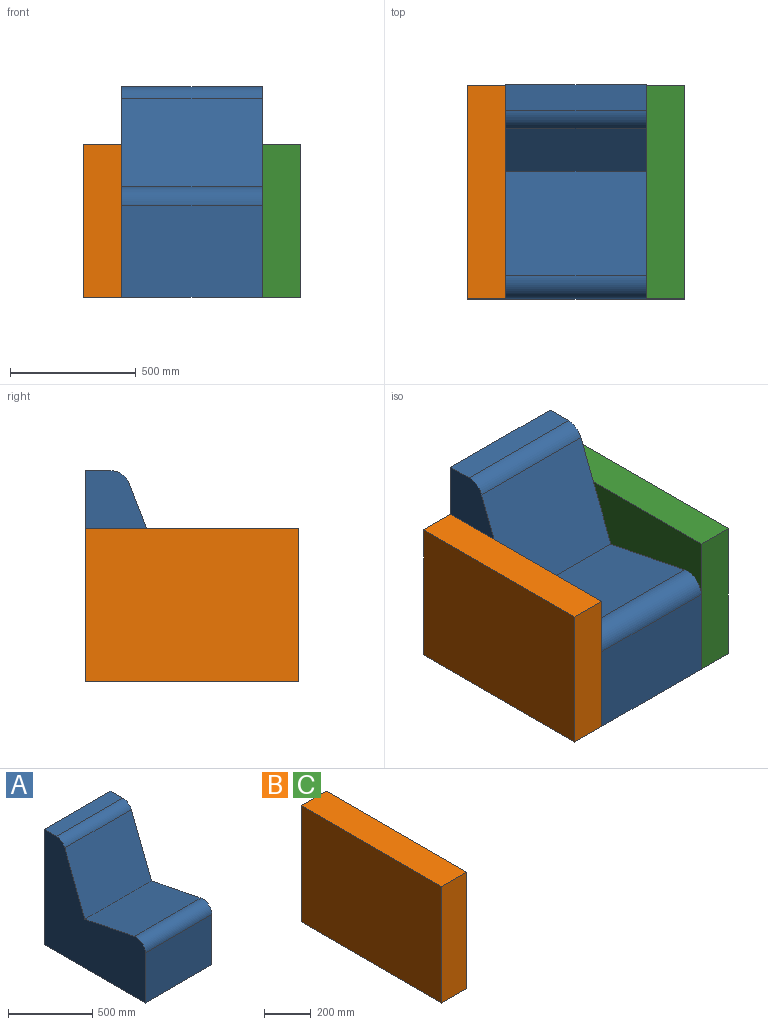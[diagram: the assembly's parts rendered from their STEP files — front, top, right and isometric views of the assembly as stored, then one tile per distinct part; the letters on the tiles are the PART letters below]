
ASSEMBLY  parts=3 mates=3
PART A: 10 faces, bbox 558.8x850.9x838.2 mm
  f0: plane 558.8x416.86mm, normal (0,0.2,0.98), area 237552.2mm2, adj f1,f7,f8,f9
  f1: cylinder r=76.2mm len=558.8mm, axis (-1,0,0), area 75290.6mm2, adj f0,f2,f8,f9
  f2: plane 558.8x364.25mm, normal (0,-1,0), area 203543.4mm2, adj f1,f3,f8,f9
  f3: plane 850.9x558.8mm, normal (0,0,-1), area 475482.9mm2, adj f2,f4,f8,f9
  f4: plane 838.2x558.8mm, normal (0,1,0), area 468386.2mm2, adj f3,f5,f8,f9
  f5: plane 558.8x102.58mm, normal (0,0,1), area 57320.5mm2, adj f4,f6,f8,f9
  f6: cylinder r=76.2mm len=558.8mm, axis (-1,0,0), area 51048.5mm2, adj f5,f7,f8,f9
  f7: plane 558.8x434.09mm, normal (0,-0.93,0.36), area 260372.8mm2, adj f0,f6,f8,f9
  f8: plane 850.9x838.2mm, normal (1,0,0), area 446008mm2, adj f0,f1,f2,f3,f4,f5,f6,f7
  f9: plane 850.9x838.2mm, normal (-1,0,0), area 446008mm2, adj f0,f1,f2,f3,f4,f5,f6,f7
PART B: 6 faces, bbox 152.4x850.9x609.6 mm
  f0: plane 850.9x152.4mm, normal (0,0,-1), area 129677.2mm2, adj f1,f3,f4,f5
  f1: plane 609.6x152.4mm, normal (0,1,0), area 92903mm2, adj f0,f2,f4,f5
  f2: plane 850.9x152.4mm, normal (0,0,1), area 129677.2mm2, adj f1,f3,f4,f5
  f3: plane 609.6x152.4mm, normal (0,-1,0), area 92903mm2, adj f0,f2,f4,f5
  f4: plane 850.9x609.6mm, normal (-1,0,0), area 518708.6mm2, adj f0,f1,f2,f3
  f5: plane 850.9x609.6mm, normal (1,0,0), area 518708.6mm2, adj f0,f1,f2,f3
PART C: same geometry as B
PLACE A at identity fixed
PLACE B t=(-279.4,0,0)mm
PLACE C t=(431.8,0,0)mm
MATE planar B.f0 <-> A.f3  axis (0,0,-1) through (-355.6,-425.45,0)mm
MATE planar B.f5 <-> A.f9  axis (1,0,0) through (-279.4,-425.45,304.8)mm
MATE planar B.f1 <-> A.f4  axis (0,1,0) through (-355.6,0,304.8)mm
